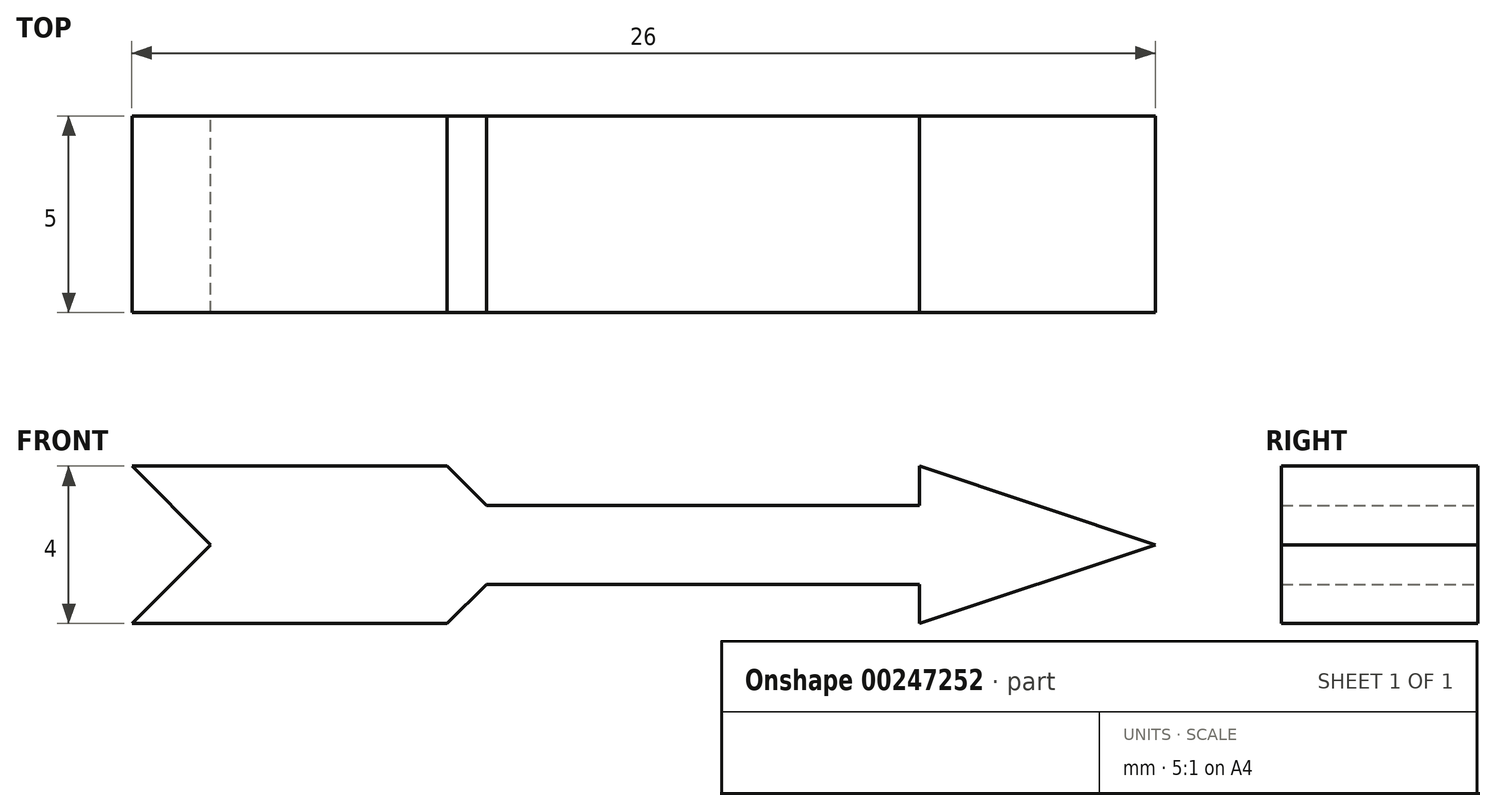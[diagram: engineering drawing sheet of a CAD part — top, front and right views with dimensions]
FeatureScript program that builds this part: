
annotation { "Feature Type Name" : "Feature", "Feature Type Description" : "" }
export const myFeature = defineFeature(function(context is Context, id is Id, definition is map)
    precondition{}
    {
        {
            var Q0;
            Q0=qCreatedBy(makeId("Front.planeOp"),FACE);
            var sketch = newSketch(context, id + "F0", { "sketchPlane" : qUnion([Q0])});
            skLineSegment(sketch, "E0", {"start": v(-15.16, 0) * mm, "end": v(15.12, 0) * mm, "construction": true});
            skLineSegment(sketch, "E1", {"start": v(-12.5, 0) * mm, "end": v(-14.5, 2) * mm});
            skLineSegment(sketch, "E2", {"start": v(-14.5, 2) * mm, "end": v(-6.5, 2) * mm});
            skLineSegment(sketch, "E3", {"start": v(-6.5, 2) * mm, "end": v(-5.5, 1) * mm});
            skLineSegment(sketch, "E4", {"start": v(-5.5, 1) * mm, "end": v(5.5, 1) * mm});
            skLineSegment(sketch, "E5", {"start": v(5.5, 1) * mm, "end": v(5.5, 2) * mm});
            skLineSegment(sketch, "E6", {"start": v(5.5, 2) * mm, "end": v(11.5, 0) * mm});
            skLineSegment(sketch, "E7.MirrorCS", {"start": v(5.5, -1) * mm, "end": v(5.5, -2) * mm});
            skLineSegment(sketch, "E8.MirrorCS", {"start": v(-12.5, 0) * mm, "end": v(-14.5, -2) * mm});
            skLineSegment(sketch, "E9.MirrorCS", {"start": v(5.5, -2) * mm, "end": v(11.5, 0) * mm});
            skLineSegment(sketch, "E10.MirrorCS", {"start": v(-14.5, -2) * mm, "end": v(-6.5, -2) * mm});
            skLineSegment(sketch, "E11.MirrorCS", {"start": v(-5.5, -1) * mm, "end": v(5.5, -1) * mm});
            skLineSegment(sketch, "E12.MirrorCS", {"start": v(-6.5, -2) * mm, "end": v(-5.5, -1) * mm});
            skSolve(sketch);
        }
        {
            var Q0;
            Q0 = qSketchRegion(id + "F0", true);
            extrude(context, id + "F1", {"entities" : qUnion([Q0]), "depth" : 5 * mm});
        }
    });
